# Revit family: Plumbing-Fix_Sanitary-Cabinet_Stern_BTM-Faucet
name_source: partatom
category: Plumbing Fixtures
revit_build: Autodesk Revit 2015 (Build: 20140606_1530(x64)
units: mm (PartAtom-declared; Revit-internal decimal feet)

## types (4) — shared parameters
Assembly Code = D2090900
Body Construction = Brass
CW Connection = Yes
CWFU = 1
Default Elevation = 0' - 0"
HW Connection = Yes
HWFU = 1
Manufacturer = Stern Engineering
Manufacturer Website = http://www.sternfaucets.com
Operating Pressure Range = 7.26 - 116 PSI  ;  0.5 - 8 bar
Operating Temperature Range = Up to 149 F / 65 C
Piping_Inlet Diameter = 1"
Product Data = http://www.arcat.com
Revision = R1_2018-04
Sales Information = http://www.sternfaucets.com
URL = http://www.sternfaucets.com
Vent Connection = No
Warranty Duration (Years) = 2
Waste Connection = No
zero-valued in all types: Cost, Expected Lifespan (Years), Maintenance Schedule (Months), WFU

## per-type parameters (varying)
| type | Description | Model | Piping_Flow | Power Supply |
| Battery Pack 1.58 GPM | Stern Concealed Touchless Faucet - BTM B as Specified | BTM B | 2 GPM | 9V Battery Pack |
| Battery Pack 0.5 GPM | Stern Concealed Touchless Faucet - BTM B as Specified | BTM B | 1 GPM | 9V Battery Pack |
| Transformer 1.58 GPM | Stern Concealed Touchless Faucet - BTM E as Specified | BTM E | 2 GPM | 9V Transformer |
| Transformer 0.5 GPM | Stern Concealed Touchless Faucet - BTM E as Specified | BTM E | 1 GPM | 9V Transformer |

## geometry (parser evidence)
native form markers: Sweep x5
no freeform markers — native parametric forms only
